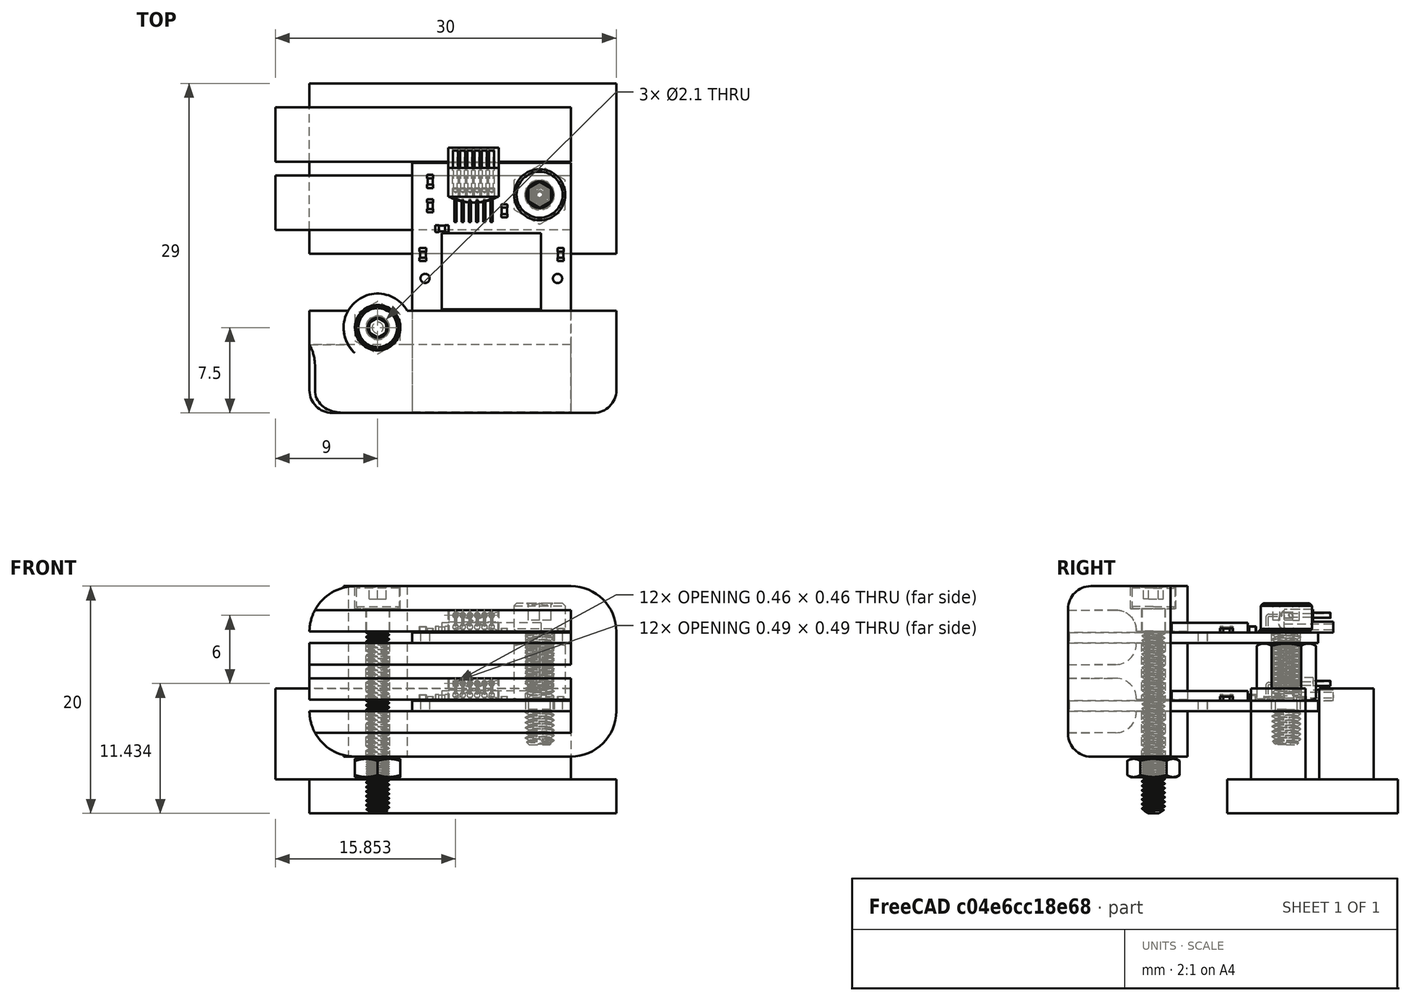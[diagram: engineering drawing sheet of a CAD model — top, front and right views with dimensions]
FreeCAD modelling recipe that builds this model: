
FCSTD DOCUMENT  (FreeCAD 0.16R6705 (Git))
Label: HeadstageAssembly
License: All rights reserved
LicenseURL: http://en.wikipedia.org/wiki/All_rights_reserved
objects: Part::Feature×42, Part::Extrusion×12, Part::Part2DObjectPython×10, Part::Cut×4, Part::Fillet×3, Part::Cylinder×3, Part::MultiFuse×3, Part::Compound×2
note: 79 computed .brp shape members not serialized (recipe doc carries the construction recipe); baked Part::Feature solids carry a one-line shape summary decoded from their .brp

FEATURE [Part::Part2DObjectPython] Rectangle  # Draft 2D object (typed FeaturePython)
  ChamferSize = 0
  Columns = 1
  FilletRadius = 0
  Height = -15
  Length = 27
  MakeFace = true
  Placement = pos=(-20,20,0) rot=(0,0,1;0rad)
  Rows = 1
FEATURE [Part::Extrusion] Extrude
  Base = -> Rectangle
  Dir = (0,0,9)
  Solid = true
FEATURE [Part::Extrusion] Extrude001
  Base = -> Rectangle
  Dir = (0,0,3)
  Solid = true
FEATURE [Part::Fillet] Fillet
  Base = -> Extrude
  Edges = 4 edges r=4: [Edge1,Edge2,Edge5,Edge8]
FEATURE [Part::Part2DObjectPython] Rectangle001  # Draft 2D object (typed FeaturePython)
  ChamferSize = 0
  Columns = 1
  FilletRadius = 0
  Height = 1
  Length = 26
  MakeFace = true
  Placement = pos=(-23,16,0) rot=(0,0,1;0rad)
  Rows = 1
FEATURE [Part::Extrusion] Extrude002
  Base = -> Rectangle001
  Dir = (0,0,-20)
  Placement = pos=(0,-1,10) rot=(0,0,1;0rad)
  Solid = true
FEATURE [Part::Part2DObjectPython] Rectangle002  # Draft 2D object (typed FeaturePython)
  ChamferSize = 0
  Columns = 1
  FilletRadius = 0
  Height = -1
  Length = 26
  MakeFace = true
  Placement = pos=(-23,10,0) rot=(0,0,1;0rad)
  Rows = 1
FEATURE [Part::Extrusion] Extrude004
  Base = -> Rectangle002
  Dir = (0,0,20)
  Placement = pos=(0,0,-4) rot=(0,0,1;0rad)
  Solid = true
FEATURE [Part::Part2DObjectPython] Rectangle003  # Draft 2D object (typed FeaturePython)
  ChamferSize = 0
  Columns = 1
  FilletRadius = 0
  Height = -1.4
  Length = 15
  MakeFace = true
  Placement = pos=(-13,22,0) rot=(0,0,1;0rad)
  Rows = 1
FEATURE [Part::Part2DObjectPython] Rectangle004  # Draft 2D object (typed FeaturePython)
  ChamferSize = 0
  Columns = 1
  FilletRadius = 0
  Height = 4.8
  Length = 26
  MakeFace = true
  Placement = pos=(-23,13.1,0) rot=(0,0,1;0rad)
  Rows = 1
FEATURE [Part::Extrusion] Extrude005
  Base = -> Rectangle004
  Dir = (0,0,-8)
  Placement = pos=(0,0,11) rot=(0,0,1;0rad)
  Solid = true
FEATURE [Part::Extrusion] Extrude006
  Base = -> Rectangle004
  Dir = (0,0,-8)
  Placement = pos=(0,0,11) rot=(0,0,1;0rad)
  Solid = true
FEATURE [Part::Part2DObjectPython] Rectangle005  # Draft 2D object (typed FeaturePython)
  ChamferSize = 0
  Columns = 1
  FilletRadius = 0
  Height = -4.8
  Length = 26
  MakeFace = true
  Placement = pos=(-23,11.9,0) rot=(0,0,1;0rad)
  Rows = 1
FEATURE [Part::Extrusion] Extrude007
  Base = -> Rectangle005
  Dir = (0,0,8)
  Placement = pos=(0,0,3) rot=(0,0,1;0rad)
  Solid = true
FEATURE [Part::Extrusion] Extrude008
  Base = -> Rectangle005
  Dir = (0,0,8)
  Placement = pos=(0,0,3) rot=(0,0,1;0rad)
  Solid = true
FEATURE [Part::Cylinder] Cylinder001
  Angle = 360
  Height = 15
  Placement = pos=(-14,20,1.5) rot=(1,0,0;1.5708rad)
  Radius = 3
FEATURE [Part::Cylinder] Cylinder
  Angle = 360
  Height = 20
  Placement = pos=(-14,21,1.5) rot=(1,0,0;1.5708rad)
  Radius = 1.05
FEATURE [Part::MultiFuse] Fusion
  Shapes = -> [Extrude002,Extrude005,Extrude004,Extrude008]
FEATURE [Part::Part2DObjectPython] Rectangle006  # Draft 2D object (typed FeaturePython)
  ChamferSize = 0
  Columns = 1
  FilletRadius = 0
  Height = 1
  Length = 26
  MakeFace = true
  Placement = pos=(-23,16,0) rot=(0,0,1;0rad)
  Rows = 1
FEATURE [Part::Extrusion] Extrude009
  Base = -> Rectangle006
  Dir = (0,0,-20)
  Placement = pos=(0,-1,10) rot=(0,0,1;0rad)
  Solid = true
FEATURE [Part::Part2DObjectPython] Rectangle007  # Draft 2D object (typed FeaturePython)
  ChamferSize = 0
  Columns = 1
  FilletRadius = 0
  Height = -1
  Length = 26
  MakeFace = true
  Placement = pos=(-23,10,0) rot=(0,0,1;0rad)
  Rows = 1
FEATURE [Part::Extrusion] Extrude010
  Base = -> Rectangle007
  Dir = (0,0,20)
  Placement = pos=(0,0,-4) rot=(0,0,1;0rad)
  Solid = true
FEATURE [Part::Part2DObjectPython] Rectangle008  # Draft 2D object (typed FeaturePython)
  ChamferSize = 0
  Columns = 1
  FilletRadius = 0
  Height = 4.8
  Length = 26
  MakeFace = true
  Placement = pos=(-23,13.1,0) rot=(0,0,1;0rad)
  Rows = 1
FEATURE [Part::Extrusion] Extrude011
  Base = -> Rectangle008
  Dir = (0,0,-8)
  Placement = pos=(0,0,11) rot=(0,0,1;0rad)
  Solid = true
FEATURE [Part::Part2DObjectPython] Rectangle009  # Draft 2D object (typed FeaturePython)
  ChamferSize = 0
  Columns = 1
  FilletRadius = 0
  Height = -4.8
  Length = 26
  MakeFace = true
  Placement = pos=(-23,11.9,0) rot=(0,0,1;0rad)
  Rows = 1
FEATURE [Part::Extrusion] Extrude012
  Base = -> Rectangle009
  Dir = (0,0,8)
  Placement = pos=(0,0,3) rot=(0,0,1;0rad)
  Solid = true
FEATURE [Part::MultiFuse] Fusion001
  Shapes = -> [Extrude009,Extrude011,Extrude010,Extrude012]
FEATURE [Part::Cut] Cut
  Base = -> Fillet
  Tool = -> Fusion
FEATURE [Part::Fillet] Fillet001
  Base = -> Cut
  Edges = 4 edges r=1.8: [Edge61,Edge64,Edge71,Edge73]
FEATURE [Part::Cut] Cut001
  Base = -> Cylinder001
  Tool = -> Fusion001
FEATURE [Part::MultiFuse] Fusion002
  Shapes = -> [Cut001,Fillet001]
FEATURE [Part::Cut] Cut002
  Base = -> Fusion002
  Placement = pos=(0,0,0) rot=(1,0,0;1.5708rad)
  Tool = -> Cylinder
FEATURE [Part::Cylinder] Cylinder002
  Angle = 360
  Height = 2
  Placement = pos=(-14,-1.5,18) rot=(0,0,1;0rad)
  Radius = 2
FEATURE [Part::Cut] Cut003
  Base = -> Cut002
  Tool = -> Cylinder002
FEATURE [Part::Feature] Part__Feature  label="SteelSocketScrew_M2_18mm"
  Placement = pos=(-14,-1.5,0) rot=(1,0,0;3.14159rad)
  shape: bbox 3.801 x 3.801 x 20.02 mm, 191 faces (baked)
FEATURE [Part::Feature] Part__Feature001  label="SteelNut_M2"
  Placement = pos=(-14,-1.5,4) rot=(0,0,1;0rad)
  shape: bbox 4.619 x 4.619 x 1.951 mm, 45 faces (baked)
FEATURE [Part::Feature] Part__Feature002  label="rhd2164_headstage1"
  shape: bbox 13.97 x 21.91 x 0.91 mm, 12 faces (baked)
FEATURE [Part::Feature] Part__Feature003  label="A79623-001"
  Placement = pos=(8.5598,2.9845,0.91) rot=(1,0,0;1.5708rad)
  shape: bbox 4.445 x 6.528 x 2.052 mm, 250 faces (baked)
FEATURE [Part::Feature] Part__Feature004  label="A79025-001"
  Placement = pos=(5.715,20.9575,2.688) rot=(0,0,1;0rad)
  shape: bbox 13.11 x 7.444 x 2.091 mm, 834 faces, 0 solids (baked)
FEATURE [Part::Feature] Part__Feature005  label="A79025-002"
  Placement = pos=(5.715,20.9575,2.688) rot=(0,0,1;0rad)
  shape: bbox 0.2479 x 0.09944 x 0.4958 mm, 2 faces, 0 solids (baked)
FEATURE [Part::Feature] Part__Feature006  label="A79025-003"
  Placement = pos=(5.715,20.9575,2.688) rot=(0,0,1;0rad)
  shape: bbox 0.2479 x 0.09944 x 0.4958 mm, 2 faces, 0 solids (baked)
FEATURE [Part::Feature] Part__Feature007  label="A79025-004"
  Placement = pos=(5.715,20.9575,2.688) rot=(0,0,1;0rad)
  shape: bbox 0.2479 x 0.09944 x 0.4958 mm, 2 faces, 0 solids (baked)
FEATURE [Part::Feature] Part__Feature008  label="A79025-005"
  Placement = pos=(5.715,20.9575,2.688) rot=(0,0,1;0rad)
  shape: bbox 0.2479 x 0.09944 x 0.4958 mm, 2 faces, 0 solids (baked)
FEATURE [Part::Feature] Part__Feature009  label="A79025-006"
  Placement = pos=(8.255,20.9575,-1.778) rot=(0,1,0;3.14159rad)
  shape: bbox 13.11 x 7.444 x 2.091 mm, 834 faces, 0 solids (baked)
FEATURE [Part::Feature] Part__Feature010  label="A79025-007"
  Placement = pos=(8.255,20.9575,-1.778) rot=(0,1,0;3.14159rad)
  shape: bbox 0.2479 x 0.09944 x 0.4958 mm, 2 faces, 0 solids (baked)
FEATURE [Part::Feature] Part__Feature011  label="A79025-008"
  Placement = pos=(8.255,20.9575,-1.778) rot=(0,1,0;3.14159rad)
  shape: bbox 0.2479 x 0.09944 x 0.4958 mm, 2 faces, 0 solids (baked)
FEATURE [Part::Feature] Part__Feature012  label="A79025-009"
  Placement = pos=(8.255,20.9575,-1.778) rot=(0,1,0;3.14159rad)
  shape: bbox 0.2479 x 0.09944 x 0.4958 mm, 2 faces, 0 solids (baked)
FEATURE [Part::Feature] Part__Feature013  label="A79025-010"
  Placement = pos=(8.255,20.9575,-1.778) rot=(0,1,0;3.14159rad)
  shape: bbox 0.2479 x 0.09944 x 0.4958 mm, 2 faces, 0 solids (baked)
FEATURE [Part::Feature] Part__Feature014  label="RHD2164_epoxy_coated"
  Placement = pos=(2.6416,6.1976,0.91) rot=(1,0,0;1.5708rad)
  shape: bbox 8.712 x 6.68 x 0.8509 mm, 6 faces (baked)
FEATURE [Part::Feature] Part__Feature015  label="0402r_1430758"
  Placement = pos=(12.3825,3.7719,0.91) rot=(0,0,1;1.5708rad)
  shape: bbox 0.55 x 1.15 x 0.4 mm, 18 faces (baked)
FEATURE [Part::Feature] Part__Feature016  label="0402r_1430759"
  Placement = pos=(12.3825,1.6256,0.91) rot=(0,0,1;1.5708rad)
  shape: bbox 0.55 x 1.15 x 0.4 mm, 18 faces (baked)
FEATURE [Part::Feature] Part__Feature017  label="0402r_1430760"
  Placement = pos=(5.8547,4.2164,0.91) rot=(0,0,1;1.5708rad)
  shape: bbox 0.55 x 1.15 x 0.4 mm, 18 faces (baked)
FEATURE [Part::Feature] Part__Feature018  label="0402r_1430761"
  Placement = pos=(0.9017,8.0645,0.91) rot=(0,0,1;1.5708rad)
  shape: bbox 0.55 x 1.15 x 0.4 mm, 18 faces (baked)
FEATURE [Part::Feature] Part__Feature019  label="0402c_2320560"
  Placement = pos=(11.3455,5.7737,0.91) rot=(0,0,1;0rad)
  shape: bbox 1.15 x 0.6 x 0.55 mm, 18 faces (baked)
FEATURE [Part::Feature] Part__Feature020  label="0402c_2320561"
  Placement = pos=(13.0175,8.0645,0.91) rot=(0,0,1;1.5708rad)
  shape: bbox 0.6 x 1.15 x 0.55 mm, 18 faces (baked)
FEATURE [Part::Compound] Compound  label="Intan_64ch_A"
  Links = -> [Part__Feature002,Part__Feature006,Part__Feature011,Part__Feature008,Part__Feature003,Part__Feature009,Part__Feature015,Part__Feature005,Part__Feature016,Part__Feature018,Part__Feature019,Part__Feature004,Part__Feature012,Part__Feature007,Part__Feature017,Part__Feature013,Part__Feature014,Part__Feature020,Part__Feature010]
  Placement = pos=(3,13,9) rot=(0,0,1;3.14159rad)
FEATURE [Part::Feature] Part__Feature021  label="rhd2164_headstage002"
  shape: bbox 13.97 x 21.91 x 0.91 mm, 12 faces (baked)
FEATURE [Part::Feature] Part__Feature022  label="A79623-002"
  Placement = pos=(8.5598,2.9845,0.91) rot=(1,0,0;1.5708rad)
  shape: bbox 4.445 x 6.528 x 2.052 mm, 250 faces (baked)
FEATURE [Part::Feature] Part__Feature023  label="A79025-011"
  Placement = pos=(5.715,20.9575,2.688) rot=(0,0,1;0rad)
  shape: bbox 13.11 x 7.444 x 2.091 mm, 834 faces, 0 solids (baked)
FEATURE [Part::Feature] Part__Feature024  label="A79025-012"
  Placement = pos=(5.715,20.9575,2.688) rot=(0,0,1;0rad)
  shape: bbox 0.2479 x 0.09944 x 0.4958 mm, 2 faces, 0 solids (baked)
FEATURE [Part::Feature] Part__Feature025  label="A79025-013"
  Placement = pos=(5.715,20.9575,2.688) rot=(0,0,1;0rad)
  shape: bbox 0.2479 x 0.09944 x 0.4958 mm, 2 faces, 0 solids (baked)
FEATURE [Part::Feature] Part__Feature026  label="A79025-014"
  Placement = pos=(5.715,20.9575,2.688) rot=(0,0,1;0rad)
  shape: bbox 0.2479 x 0.09944 x 0.4958 mm, 2 faces, 0 solids (baked)
FEATURE [Part::Feature] Part__Feature027  label="A79025-015"
  Placement = pos=(5.715,20.9575,2.688) rot=(0,0,1;0rad)
  shape: bbox 0.2479 x 0.09944 x 0.4958 mm, 2 faces, 0 solids (baked)
FEATURE [Part::Feature] Part__Feature028  label="A79025-016"
  Placement = pos=(8.255,20.9575,-1.778) rot=(0,1,0;3.14159rad)
  shape: bbox 13.11 x 7.444 x 2.091 mm, 834 faces, 0 solids (baked)
FEATURE [Part::Feature] Part__Feature029  label="A79025-017"
  Placement = pos=(8.255,20.9575,-1.778) rot=(0,1,0;3.14159rad)
  shape: bbox 0.2479 x 0.09944 x 0.4958 mm, 2 faces, 0 solids (baked)
FEATURE [Part::Feature] Part__Feature030  label="A79025-018"
  Placement = pos=(8.255,20.9575,-1.778) rot=(0,1,0;3.14159rad)
  shape: bbox 0.2479 x 0.09944 x 0.4958 mm, 2 faces, 0 solids (baked)
FEATURE [Part::Feature] Part__Feature031  label="A79025-019"
  Placement = pos=(8.255,20.9575,-1.778) rot=(0,1,0;3.14159rad)
  shape: bbox 0.2479 x 0.09944 x 0.4958 mm, 2 faces, 0 solids (baked)
FEATURE [Part::Feature] Part__Feature032  label="A79025-020"
  Placement = pos=(8.255,20.9575,-1.778) rot=(0,1,0;3.14159rad)
  shape: bbox 0.2479 x 0.09944 x 0.4958 mm, 2 faces, 0 solids (baked)
FEATURE [Part::Feature] Part__Feature033  label="RHD2164_epoxy_coated001"
  Placement = pos=(2.6416,6.1976,0.91) rot=(1,0,0;1.5708rad)
  shape: bbox 8.712 x 6.68 x 0.8509 mm, 6 faces (baked)
FEATURE [Part::Feature] Part__Feature034  label="0402r_1430762"
  Placement = pos=(12.3825,3.7719,0.91) rot=(0,0,1;1.5708rad)
  shape: bbox 0.55 x 1.15 x 0.4 mm, 18 faces (baked)
FEATURE [Part::Feature] Part__Feature035  label="0402r_1430763"
  Placement = pos=(12.3825,1.6256,0.91) rot=(0,0,1;1.5708rad)
  shape: bbox 0.55 x 1.15 x 0.4 mm, 18 faces (baked)
FEATURE [Part::Feature] Part__Feature036  label="0402r_1430764"
  Placement = pos=(5.8547,4.2164,0.91) rot=(0,0,1;1.5708rad)
  shape: bbox 0.55 x 1.15 x 0.4 mm, 18 faces (baked)
FEATURE [Part::Feature] Part__Feature037  label="0402r_1430765"
  Placement = pos=(0.9017,8.0645,0.91) rot=(0,0,1;1.5708rad)
  shape: bbox 0.55 x 1.15 x 0.4 mm, 18 faces (baked)
FEATURE [Part::Feature] Part__Feature038  label="0402c_2320562"
  Placement = pos=(11.3455,5.7737,0.91) rot=(0,0,1;0rad)
  shape: bbox 1.15 x 0.6 x 0.55 mm, 18 faces (baked)
FEATURE [Part::Feature] Part__Feature039  label="0402c_2320563"
  Placement = pos=(13.0175,8.0645,0.91) rot=(0,0,1;1.5708rad)
  shape: bbox 0.6 x 1.15 x 0.55 mm, 18 faces (baked)
FEATURE [Part::Compound] Compound001  label="Intan_64ch_B"
  Links = -> [Part__Feature021,Part__Feature025,Part__Feature030,Part__Feature027,Part__Feature022,Part__Feature028,Part__Feature034,Part__Feature024,Part__Feature035,Part__Feature037,Part__Feature038,Part__Feature023,Part__Feature031,Part__Feature026,Part__Feature036,Part__Feature032,Part__Feature033,Part__Feature039,Part__Feature029]
  Placement = pos=(3,13,15) rot=(0,0,1;3.14159rad)
FEATURE [Part::Feature] Part__Feature040  label="NylonSpacer_M2.5_5mm"
  Placement = pos=(0.25,10.2,10.5) rot=(0,1,0;1.5708rad)
  shape: bbox 5.197 x 5.197 x 9.238 mm, 74 faces (baked)
FEATURE [Part::Feature] Part__Feature041  label="NylonScrew_M2.5_5mm"
  Placement = pos=(0.25,10.2,11) rot=(0,1,0;3.14159rad)
  shape: bbox 4.501 x 4.501 x 7.519 mm, 71 faces (baked)
FEATURE [Part::Fillet] Fillet002
  Base = -> Cut003
  Edges = 8 edges r=2: [Edge1,Edge2,Edge3,Edge4,Edge5,Edge6,Edge12,Edge18]
